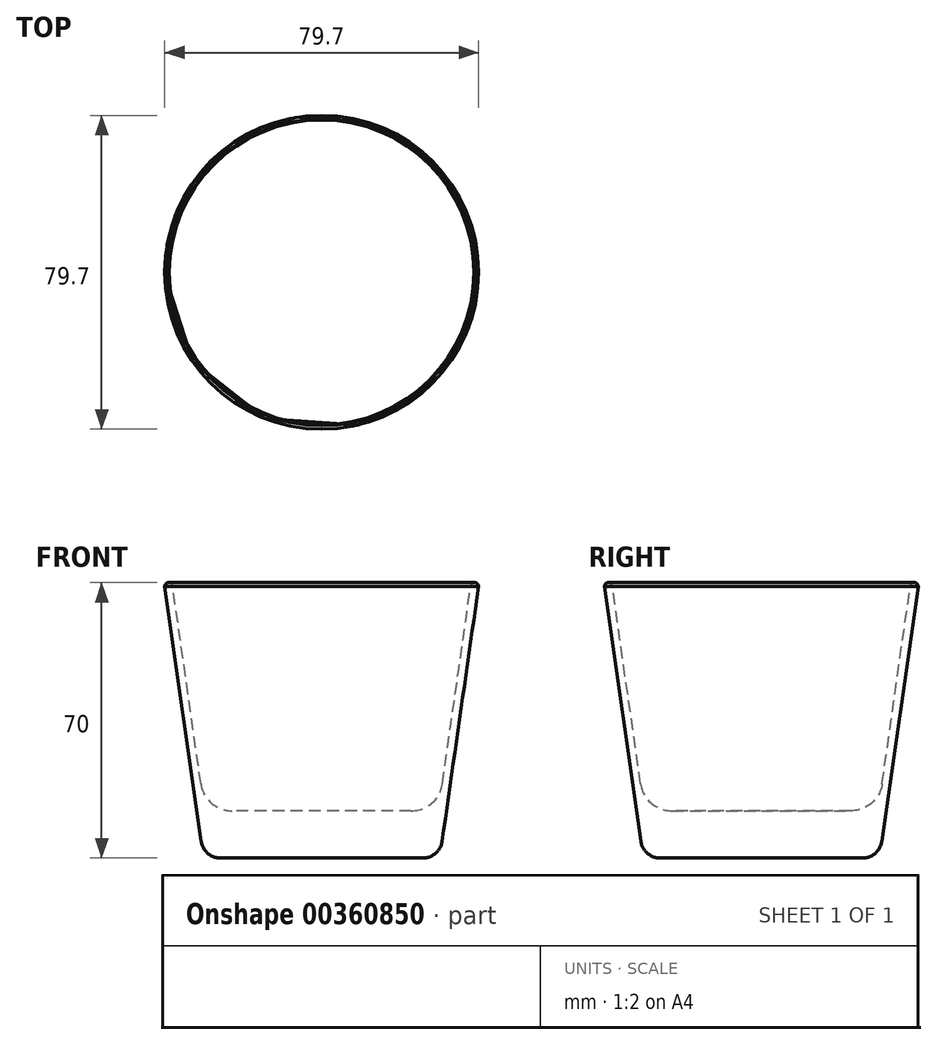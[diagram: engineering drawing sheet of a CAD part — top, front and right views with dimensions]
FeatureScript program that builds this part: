
annotation { "Feature Type Name" : "Feature", "Feature Type Description" : "" }
export const myFeature = defineFeature(function(context is Context, id is Id, definition is map)
    precondition{}
    {
        {
            var Q0;
            Q0=qCreatedBy(makeId("Front.planeOp"),FACE);
            var sketch = newSketch(context, id + "F0", { "sketchPlane" : qUnion([Q0])});
            skLineSegment(sketch, "E0", {"start": v(0, 0) * mm, "end": v(0, 70) * mm, "construction": true});
            skLineSegment(sketch, "E1", {"start": v(0, 0) * mm, "end": v(25.66, 0) * mm});
            skLineSegment(sketch, "E2", {"start": v(30.61, 4.3) * mm, "end": v(39.85, 68.98) * mm});
            skPoint(sketch, "E3.visualSharp", {"position": v(30, 0) * mm});
            skArc(sketch, "E3.filletArc", {"start": v(25.66, 0) * mm, "mid": v(28.94, 1.22) * mm, "end": v(30.61, 4.3) * mm});
            skLineSegment(sketch, "E4.0", {"start": v(30.68, 18.87) * mm, "end": v(37.86, 69.15) * mm});
            skLineSegment(sketch, "E5.0", {"start": v(0, 12) * mm, "end": v(22.76, 12) * mm});
            skArc(sketch, "E6.filletArc", {"start": v(22.76, 12) * mm, "mid": v(28, 13.96) * mm, "end": v(30.68, 18.87) * mm});
            skLineSegment(sketch, "E7", {"start": v(38.99, 70) * mm, "end": v(38.71, 70) * mm});
            skArc(sketch, "E8", {"start": v(39.82, 68.75) * mm, "mid": v(39.05, 69.99) * mm, "end": v(37.86, 69.15) * mm});
            skPoint(sketch, "E8.first.point", {"position": v(37.86, 69.15) * mm});
            skPoint(sketch, "E8.second.point", {"position": v(38.99, 70) * mm});
            skPoint(sketch, "E8.third.point", {"position": v(39.85, 68.98) * mm});
            skPoint(sketch, "E9.orphan", {"position": v(37.98, 70) * mm});
            skPoint(sketch, "E10.orphan", {"position": v(40, 70) * mm});
            skLineSegment(sketch, "E11", {"start": v(0, 12) * mm, "end": v(0, 0) * mm});
            skSolve(sketch);
        }
        {
            var Q0;
            Q0=makeQuery(id+"F0.imprint","IMPRINT",FACE,{"disambiguationData":[TD([[makeQuery(id+"F0.imprint","IMPRINT",EDGE,{"derivedFrom":sQuery(id+"F0.wireOp",EDGE,"E1")}),1.0]])]});
            var Q1;
            Q1=sQuery(id+"F0.wireOp",EDGE,"E11");
            revolve(context, id + "F1", {"entities" : qUnion([Q0]), "axis" : qUnion([Q1]), "revolveType" : RevolveType.FULL});
        }
    });
